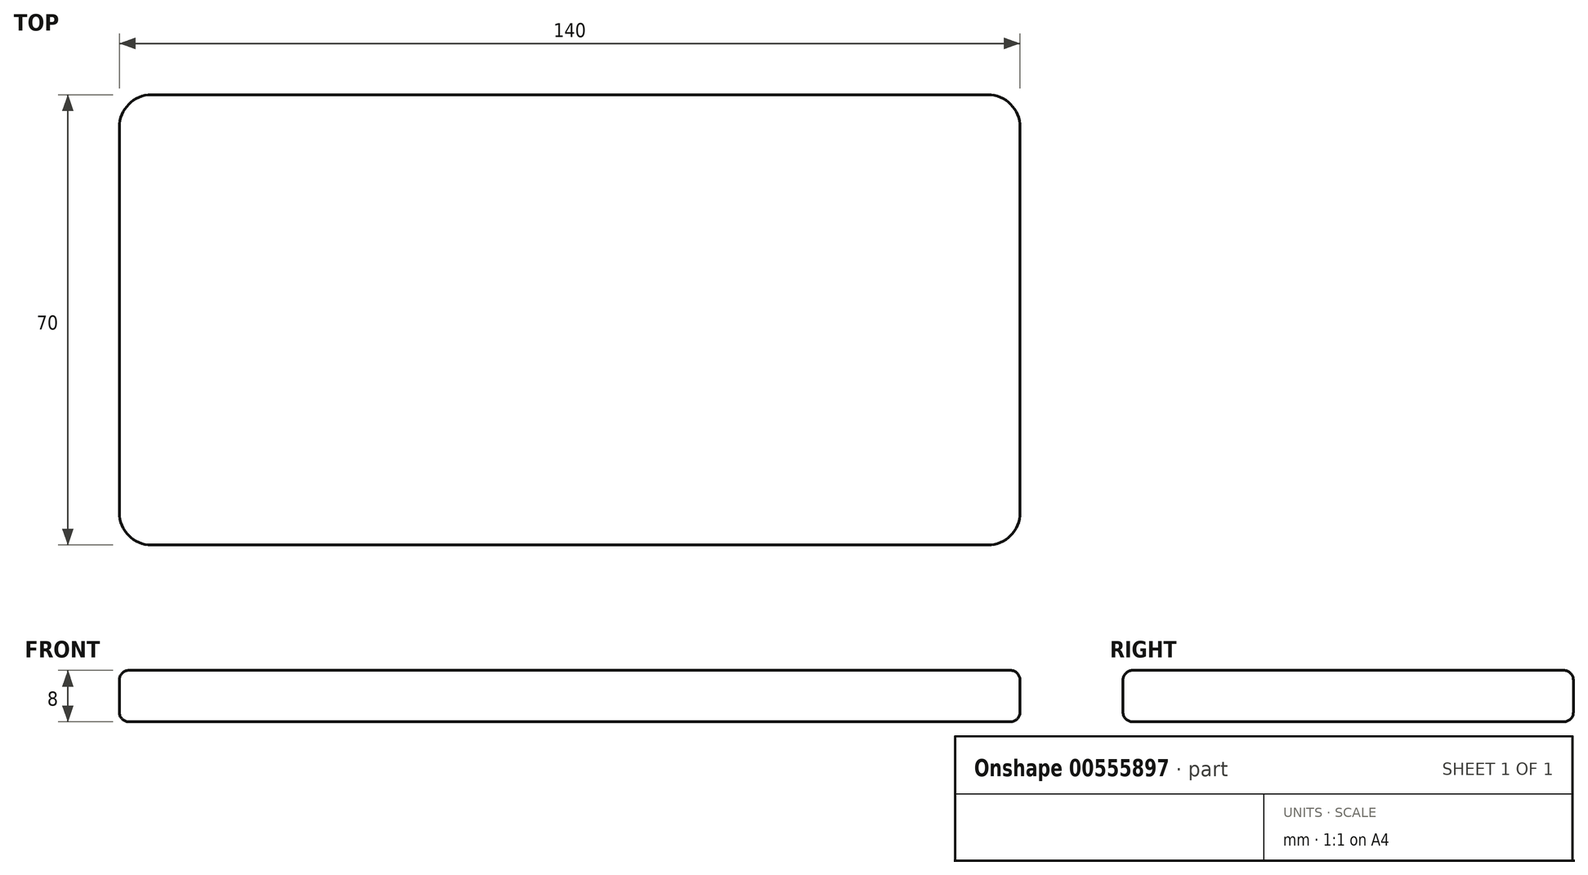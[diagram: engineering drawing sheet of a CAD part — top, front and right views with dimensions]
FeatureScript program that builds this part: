
annotation { "Feature Type Name" : "Feature", "Feature Type Description" : "" }
export const myFeature = defineFeature(function(context is Context, id is Id, definition is map)
    precondition{}
    {
        {
            var Q0;
            Q0=qCreatedBy(makeId("Top.planeOp"),FACE);
            var sketch = newSketch(context, id + "F0", { "sketchPlane" : qUnion([Q0])});
            skLineSegment(sketch, "E0.bottom", {"start": v(-52.37, 35.7) * mm, "end": v(77.63, 35.7) * mm});
            skLineSegment(sketch, "E0.top", {"start": v(-52.37, -34.3) * mm, "end": v(77.63, -34.3) * mm});
            skLineSegment(sketch, "E0.left", {"start": v(-57.37, 30.7) * mm, "end": v(-57.37, -29.3) * mm});
            skLineSegment(sketch, "E0.right", {"start": v(82.63, 30.7) * mm, "end": v(82.63, -29.3) * mm});
            skPoint(sketch, "E1.visualSharp", {"position": v(-57.37, 35.7) * mm});
            skArc(sketch, "E1.filletArc", {"start": v(-52.37, 35.7) * mm, "mid": v(-55.9, 34.24) * mm, "end": v(-57.37, 30.7) * mm});
            skPoint(sketch, "E2.visualSharp", {"position": v(-57.37, -34.3) * mm});
            skArc(sketch, "E2.filletArc", {"start": v(-57.37, -29.3) * mm, "mid": v(-55.9, -32.83) * mm, "end": v(-52.37, -34.3) * mm});
            skPoint(sketch, "E3.visualSharp", {"position": v(82.63, -34.3) * mm});
            skArc(sketch, "E3.filletArc", {"start": v(77.63, -34.3) * mm, "mid": v(81.16, -32.83) * mm, "end": v(82.63, -29.3) * mm});
            skPoint(sketch, "E4.visualSharp", {"position": v(82.63, 35.7) * mm});
            skArc(sketch, "E4.filletArc", {"start": v(82.63, 30.7) * mm, "mid": v(81.16, 34.24) * mm, "end": v(77.63, 35.7) * mm});
            skSolve(sketch);
        }
        {
            var Q0;
            Q0=makeQuery(id+"F0.imprint","IMPRINT",FACE,{"disambiguationData":[TD([[makeQuery(id+"F0.imprint","IMPRINT",EDGE,{"derivedFrom":sQuery(id+"F0.wireOp",EDGE,"E0.bottom")}),-1.0]])]});
            extrude(context, id + "F1", {"entities" : qUnion([Q0]), "depth" : 8 * mm, "offsetDistance" : 25 * mm});
        }
        {
            var Q0;
            Q0=makeQuery(id+"F1.opExtrude","CAP_FACE",FACE,{"disambiguationData":[OSD([sQuery(id+"F0.wireOp",EDGE,"E0.bottom"),sQuery(id+"F0.wireOp",EDGE,"E0.top"),sQuery(id+"F0.wireOp",EDGE,"E0.left"),sQuery(id+"F0.wireOp",EDGE,"E0.right"),sQuery(id+"F0.wireOp",EDGE,"E1.filletArc"),sQuery(id+"F0.wireOp",EDGE,"E2.filletArc"),sQuery(id+"F0.wireOp",EDGE,"E3.filletArc"),sQuery(id+"F0.wireOp",EDGE,"E4.filletArc")])],"isStart":false});
            var sketch = newSketch(context, id + "F2", { "sketchPlane" : qUnion([Q0])});
            skSolve(sketch);
        }
        {
            var Q0;
            Q0=makeQuery(id+"F1.opExtrude","CAP_FACE",FACE,{"disambiguationData":[OSD([sQuery(id+"F0.wireOp",EDGE,"E0.bottom"),sQuery(id+"F0.wireOp",EDGE,"E0.top"),sQuery(id+"F0.wireOp",EDGE,"E0.left"),sQuery(id+"F0.wireOp",EDGE,"E0.right"),sQuery(id+"F0.wireOp",EDGE,"E1.filletArc"),sQuery(id+"F0.wireOp",EDGE,"E2.filletArc"),sQuery(id+"F0.wireOp",EDGE,"E3.filletArc"),sQuery(id+"F0.wireOp",EDGE,"E4.filletArc")])],"isStart":false});
            fillet(context, id + "F3", {"entities" : qUnion([Q0]), "radius" : 1.5 * mm, "tangentPropagation" : true, "allowEdgeOverflow" : false});
        }
        {
            var Q0;
            Q0=makeQuery(id+"F1.opExtrude","CAP_FACE",FACE,{"disambiguationData":[OSD([sQuery(id+"F0.wireOp",EDGE,"E0.bottom"),sQuery(id+"F0.wireOp",EDGE,"E0.top"),sQuery(id+"F0.wireOp",EDGE,"E0.left"),sQuery(id+"F0.wireOp",EDGE,"E0.right"),sQuery(id+"F0.wireOp",EDGE,"E1.filletArc"),sQuery(id+"F0.wireOp",EDGE,"E2.filletArc"),sQuery(id+"F0.wireOp",EDGE,"E3.filletArc"),sQuery(id+"F0.wireOp",EDGE,"E4.filletArc")])],"isStart":true});
            fillet(context, id + "F4", {"entities" : qUnion([Q0]), "radius" : 1.5 * mm, "tangentPropagation" : true, "allowEdgeOverflow" : false});
        }
    });
